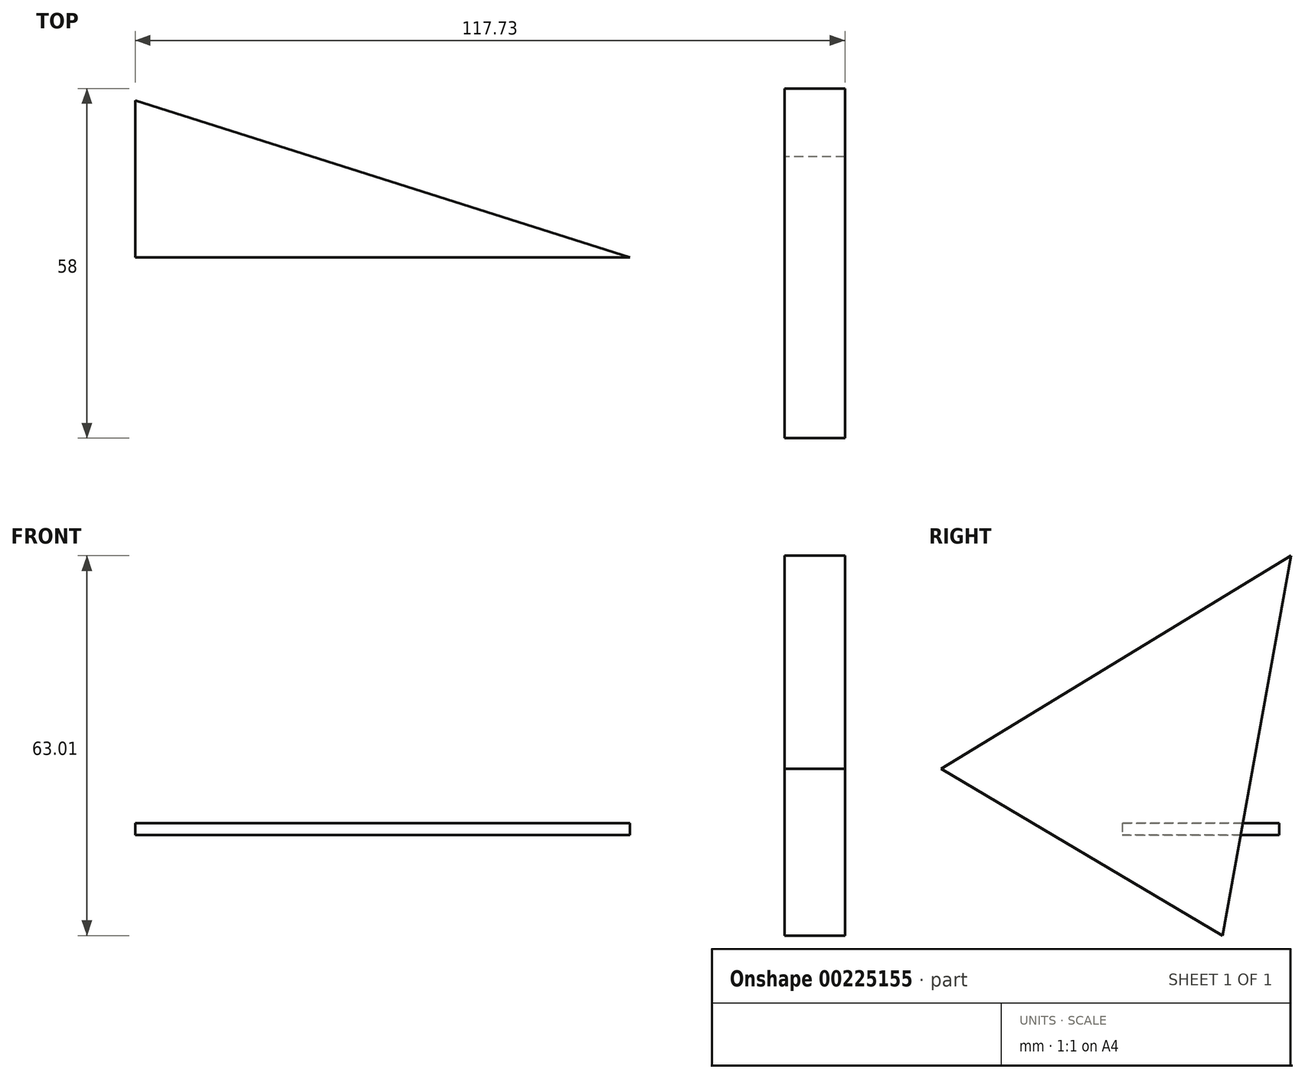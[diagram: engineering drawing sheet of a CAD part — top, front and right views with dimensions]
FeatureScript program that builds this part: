
annotation { "Feature Type Name" : "Feature", "Feature Type Description" : "" }
export const myFeature = defineFeature(function(context is Context, id is Id, definition is map)
    precondition{}
    {
        {
            var Q0;
            Q0=qCreatedBy(makeId("Top.planeOp"),FACE);
            var sketch = newSketch(context, id + "F0", { "sketchPlane" : qUnion([Q0])});
            skLineSegment(sketch, "E0", {"start": v(-107.73, 0) * mm, "end": v(-107.73, 11.84) * mm});
            skLineSegment(sketch, "E1", {"start": v(-25.64, 0) * mm, "end": v(-107.73, 0) * mm});
            skLineSegment(sketch, "E2", {"start": v(-107.73, 26.05) * mm, "end": v(-25.64, 0) * mm});
            skLineSegment(sketch, "E3", {"start": v(-107.73, 26.05) * mm, "end": v(-107.73, 11.84) * mm});
            skSolve(sketch);
        }
        {
            var Q0;
            Q0=makeQuery(id+"F0.imprint","IMPRINT",FACE,{"disambiguationData":[TD([[makeQuery(id+"F0.imprint","IMPRINT",EDGE,{"derivedFrom":sQuery(id+"F0.wireOp",EDGE,"E0")}),-1.0]])]});
            extrude(context, id + "F1", {"entities" : qUnion([Q0]), "depth" : 2 * mm});
        }
        {
            var Q0;
            Q0=qCreatedBy(makeId("Right.planeOp"),FACE);
            var sketch = newSketch(context, id + "F2", { "sketchPlane" : qUnion([Q0])});
            skLineSegment(sketch, "E4", {"start": v(28, 46.34) * mm, "end": v(16.67, -16.67) * mm});
            skLineSegment(sketch, "E5", {"start": v(16.67, -16.67) * mm, "end": v(-30, 11) * mm});
            skLineSegment(sketch, "E6", {"start": v(-30, 11) * mm, "end": v(28, 46.34) * mm});
            skSolve(sketch);
        }
        {
            var Q0;
            Q0=makeQuery(id+"F2.imprint","IMPRINT",FACE,{"disambiguationData":[TD([[makeQuery(id+"F2.imprint","IMPRINT",EDGE,{"derivedFrom":sQuery(id+"F2.wireOp",EDGE,"E4")}),-1.0]])]});
            extrude(context, id + "F3", {"entities" : qUnion([Q0]), "depth" : 10 * mm});
        }
    });
